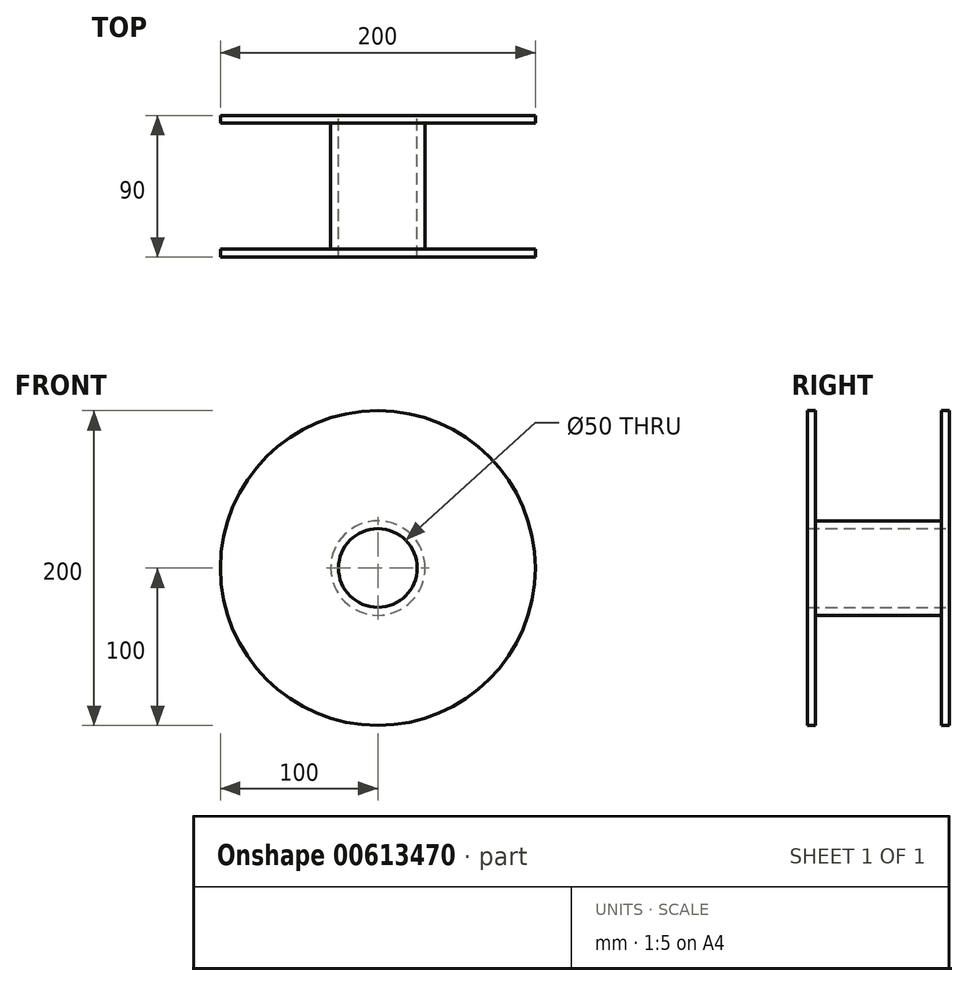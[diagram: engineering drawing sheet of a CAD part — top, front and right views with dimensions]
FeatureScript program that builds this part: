
annotation { "Feature Type Name" : "Feature", "Feature Type Description" : "" }
export const myFeature = defineFeature(function(context is Context, id is Id, definition is map)
    precondition{}
    {
        {
            var Q0;
            Q0=qCreatedBy(makeId("Front.planeOp"),FACE);
            var sketch = newSketch(context, id + "F0", { "sketchPlane" : qUnion([Q0])});
            skCircle(sketch, "E0", {"center": v(0, 0) * mm, "radius": 100 * mm});
            skCircle(sketch, "E1", {"center": v(0, 0) * mm, "radius": 25 * mm});
            skSolve(sketch);
        }
        {
            var Q0;
            Q0=makeQuery(id+"F0.imprint","IMPRINT",FACE,{"disambiguationData":[TD([[makeQuery(id+"F0.imprint","IMPRINT",EDGE,{"derivedFrom":sQuery(id+"F0.wireOp",EDGE,"E0")}),1.0]])]});
            extrude(context, id + "F1", {"entities" : qUnion([Q0]), "endBound" : BoundingType.SYMMETRIC, "depth" : 90 * mm, "offsetDistance" : 25 * mm});
        }
        {
            var Q0;
            Q0=makeQuery(id+"F1.opExtrude","SWEPT_FACE",FACE,{"disambiguationData":[OSD([sQuery(id+"F0.wireOp",EDGE,"E0")])]});
            shell(context, id + "F2", {"entities" : qUnion([Q0]), "thickness" : 5 * mm});
        }
    });
